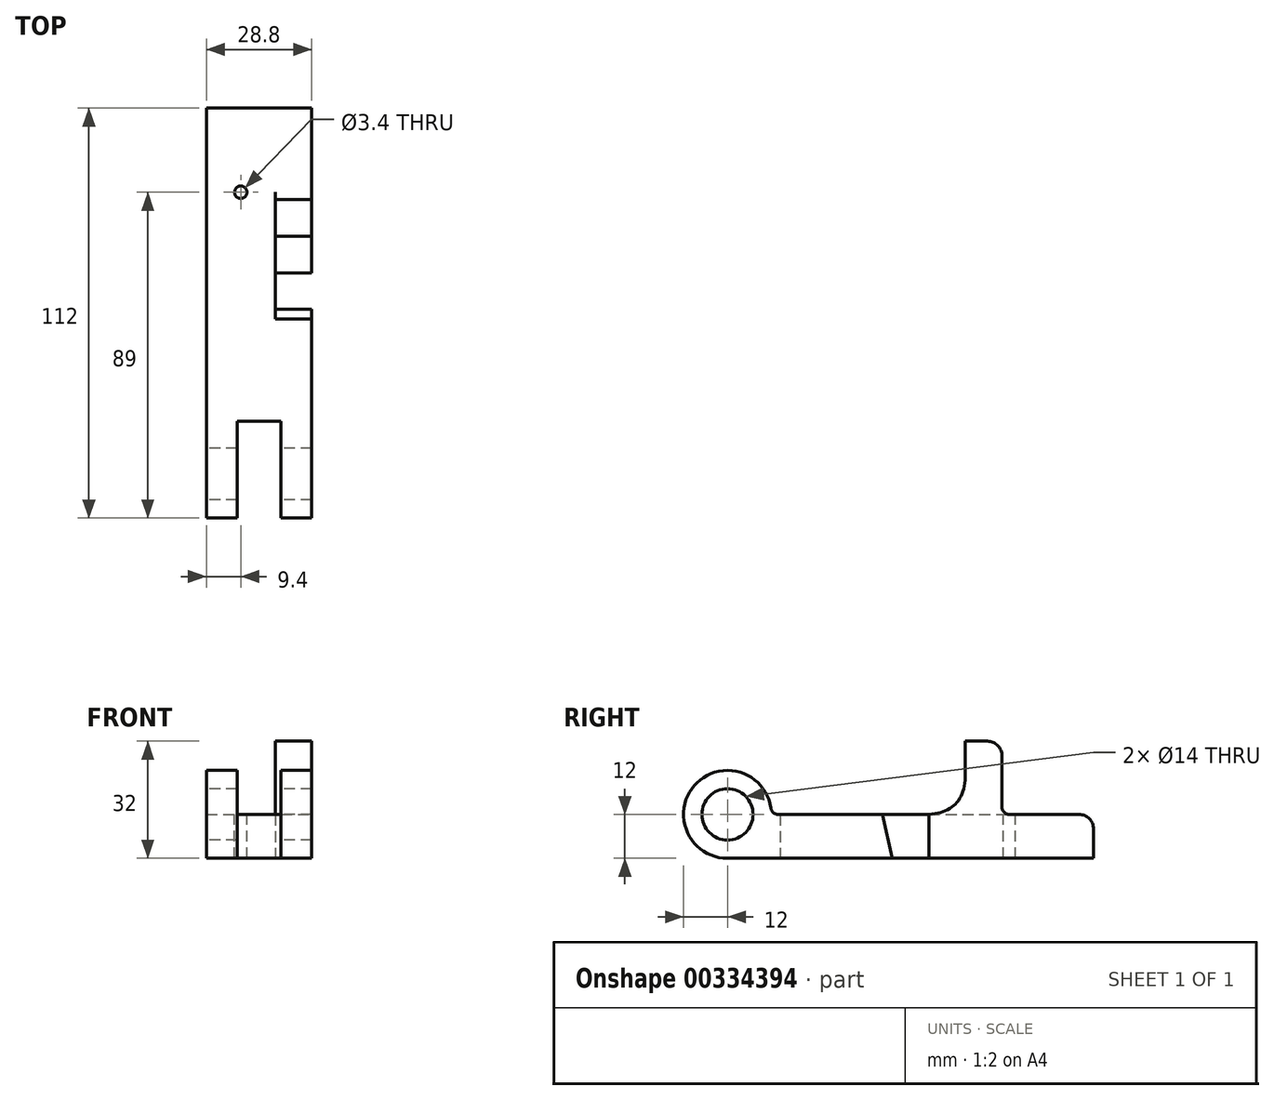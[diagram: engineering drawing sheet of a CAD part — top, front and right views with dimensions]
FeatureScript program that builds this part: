
annotation { "Feature Type Name" : "Feature", "Feature Type Description" : "" }
export const myFeature = defineFeature(function(context is Context, id is Id, definition is map)
    precondition{}
    {
        {
            var Q0;
            Q0=qCreatedBy(makeId("Right.planeOp"),FACE);
            var sketch = newSketch(context, id + "F0", { "sketchPlane" : qUnion([Q0])});
            skArc(sketch, "E0", {"start": v(12, 0) * mm, "mid": v(-8.49, 8.49) * mm, "end": v(0, -12) * mm});
            skCircle(sketch, "E1", {"center": v(0, 0) * mm, "radius": 7 * mm});
            skLineSegment(sketch, "E2", {"start": v(0, -12) * mm, "end": v(47.36, -12) * mm});
            skLineSegment(sketch, "E3", {"start": v(47.36, -12) * mm, "end": v(57.36, -12) * mm});
            skLineSegment(sketch, "E4", {"start": v(57.36, -12) * mm, "end": v(100, -12) * mm});
            skLineSegment(sketch, "E5", {"start": v(100, -12) * mm, "end": v(100, -4) * mm});
            skLineSegment(sketch, "E6", {"start": v(96, 0) * mm, "end": v(77, 0) * mm});
            skLineSegment(sketch, "E7", {"start": v(0, 12) * mm, "end": v(42.36, 12) * mm, "construction": true});
            skLineSegment(sketch, "E8", {"start": v(42.36, 0) * mm, "end": v(47.36, -12) * mm});
            skLineSegment(sketch, "E9", {"start": v(57.36, -12) * mm, "end": v(57.36, 0) * mm});
            skLineSegment(sketch, "E10", {"start": v(65, 20) * mm, "end": v(71, 20) * mm});
            skLineSegment(sketch, "E11", {"start": v(75, 16) * mm, "end": v(75, 2) * mm});
            skPoint(sketch, "E12.visualSharp", {"position": v(100, 0) * mm});
            skArc(sketch, "E12.filletArc", {"start": v(100, -4) * mm, "mid": v(98.83, -1.17) * mm, "end": v(96, 0) * mm});
            skPoint(sketch, "E13.visualSharp", {"position": v(75, 20) * mm});
            skArc(sketch, "E13.filletArc", {"start": v(75, 16) * mm, "mid": v(73.83, 18.83) * mm, "end": v(71, 20) * mm});
            skLineSegment(sketch, "E14.trimOffspring", {"start": v(57.36, 0) * mm, "end": v(12, 0) * mm});
            skPoint(sketch, "E15.visualSharp", {"position": v(75, 0) * mm});
            skArc(sketch, "E15.filletArc", {"start": v(75, 2) * mm, "mid": v(75.59, 0.59) * mm, "end": v(77, 0) * mm});
            skLineSegment(sketch, "E16", {"start": v(65, 20) * mm, "end": v(65, 0) * mm});
            skLineSegment(sketch, "E17", {"start": v(57.36, 0) * mm, "end": v(65, 0) * mm});
            skSolve(sketch);
        }
        {
            var Q0;
            {var subQ1=sQuery(id+"F0.wireOp",EDGE,"E0");Q0=makeQuery(id+"F0.imprint","IMPRINT",FACE,{"disambiguationData":[TD([[makeQuery(id+"F0.imprint","IMPRINT",EDGE,{"derivedFrom":subQ1}),1.0]])]});}
            var Q1;
            Q1=makeQuery(id+"F0.imprint","IMPRINT",FACE,{"disambiguationData":[TD([[makeQuery(id+"F0.imprint","IMPRINT",EDGE,{"derivedFrom":sQuery(id+"F0.wireOp",EDGE,"E3")}),1.0]])]});
            var Q2;
            Q2=makeQuery(id+"F0.imprint","IMPRINT",FACE,{"disambiguationData":[TD([[makeQuery(id+"F0.imprint","IMPRINT",EDGE,{"derivedFrom":sQuery(id+"F0.wireOp",EDGE,"E4")}),1.0]])]});
            extrude(context, id + "F1", {"entities" : qUnion([Q0, Q1, Q2]), "endBound" : BoundingType.SYMMETRIC, "depth" : 28.8 * mm});
        }
        {
            var Q0;
            Q0=makeQuery(id+"F1.opExtrude","SWEPT_FACE",FACE,{"disambiguationData":[OSD([sQuery(id+"F0.wireOp",EDGE,"E14.trimOffspring"),sQuery(id+"F0.wireOp",EDGE,"E17")])]});
            var sketch = newSketch(context, id + "F2", { "sketchPlane" : qUnion([Q0])});
            skLineSegment(sketch, "E18.bottom", {"start": v(6, 14.45) * mm, "end": v(-6, 14.45) * mm});
            skLineSegment(sketch, "E18.top", {"start": v(6, -14.45) * mm, "end": v(-6, -14.45) * mm});
            skLineSegment(sketch, "E18.left", {"start": v(6, 14.45) * mm, "end": v(6, -14.45) * mm});
            skLineSegment(sketch, "E18.right", {"start": v(-6, 14.45) * mm, "end": v(-6, -14.45) * mm});
            skPoint(sketch, "E18.middle", {"position": v(0, 0) * mm});
            skSolve(sketch);
        }
        {
            var Q0;
            {var subQ0=sQuery(id+"F2.wireOp",EDGE,"E18.top");Q0=makeQuery(id+"F2.imprint","IMPRINT",FACE,{"disambiguationData":[TD([[makeQuery(id+"F2.imprint","IMPRINT",EDGE,{"derivedFrom":subQ0}),-1.0]])]});}
            var Q1;
            {var subQ0=sQuery(id+"F2.wireOp",EDGE,"E18.bottom");Q1=makeQuery(id+"F2.imprint","IMPRINT",FACE,{"disambiguationData":[TD([[makeQuery(id+"F2.imprint","IMPRINT",EDGE,{"derivedFrom":subQ0}),1.0]])]});}
            extrude(context, id + "F3", {"entities" : qUnion([Q0, Q1]), "operationType" : NewBodyOperationType.REMOVE, "endBound" : BoundingType.SYMMETRIC, "depth" : 30 * mm});
        }
        {
            var Q0;
            {var subQ0=sQuery(id+"F0.wireOp",EDGE,"E0");var subQ2=sQuery(id+"F0.wireOp",EDGE,"E14.trimOffspring");Q0=makeQuery(id+"F3.boolean.opBoolean","SPLIT",EDGE,{"disambiguationData":[TD([makeQuery(id+"F3.opExtrude","SWEPT_FACE",FACE,{"disambiguationData":[OSD([sQuery(id+"F2.wireOp",EDGE,"E18.left")])]})])],"derivedFrom":makeQuery(id+"F1.opExtrude","SWEPT_EDGE",EDGE,{"disambiguationData":[OSD([subQ0,subQ2])]})});}
            var Q1;
            {var subQ0=sQuery(id+"F0.wireOp",EDGE,"E0");var subQ2=sQuery(id+"F0.wireOp",EDGE,"E14.trimOffspring");Q1=makeQuery(id+"F3.boolean.opBoolean","SPLIT",EDGE,{"disambiguationData":[TD([makeQuery(id+"F3.opExtrude","SWEPT_FACE",FACE,{"disambiguationData":[OSD([sQuery(id+"F2.wireOp",EDGE,"E18.right")])]})])],"derivedFrom":makeQuery(id+"F1.opExtrude","SWEPT_EDGE",EDGE,{"disambiguationData":[OSD([subQ0,subQ2])]})});}
            fillet(context, id + "F4", {"entities" : qUnion([Q0, Q1]), "radius" : 2 * mm, "tangentPropagation" : true, "allowEdgeOverflow" : false});
        }
        {
            var Q0;
            Q0=makeQuery(id+"F1.opExtrude","SWEPT_FACE",FACE,{"disambiguationData":[OSD([sQuery(id+"F0.wireOp",EDGE,"E6")])]});
            var sketch = newSketch(context, id + "F5", { "sketchPlane" : qUnion([Q0])});
            skLineSegment(sketch, "E19", {"start": v(-14.4, 100) * mm, "end": v(-14.4, 77) * mm, "construction": true});
            skLineSegment(sketch, "E20", {"start": v(-14.4, 100) * mm, "end": v(-14.4, 90.6) * mm, "construction": true});
            skLineSegment(sketch, "E21", {"start": v(-14.4, 77) * mm, "end": v(-5, 77) * mm});
            skCircle(sketch, "E22", {"center": v(-5, 77) * mm, "radius": 1.7 * mm});
            skSolve(sketch);
        }
        {
            var Q0;
            {var subQ0=sQuery(id+"F5.wireOp",EDGE,"E21");var subQ3=sQuery(id+"F5.wireOp",EDGE,"E22");var subQ4=makeQuery(id+"F5.imprint","INTERSECT",VERTEX,{"derivedFrom":[subQ0,subQ3]});Q0=makeQuery(id+"F5.imprint","IMPRINT",FACE,{"disambiguationData":[TD([[makeQuery(id+"F5.imprint","IMPRINT",EDGE,{"disambiguationData":[TD([[subQ4,1.0]])],"derivedFrom":subQ0}),1.0]])]});}
            var Q1;
            {var subQ0=sQuery(id+"F5.wireOp",EDGE,"E21");var subQ3=sQuery(id+"F5.wireOp",EDGE,"E22");var subQ4=makeQuery(id+"F5.imprint","INTERSECT",VERTEX,{"derivedFrom":[subQ0,subQ3]});Q1=makeQuery(id+"F5.imprint","IMPRINT",FACE,{"disambiguationData":[TD([[makeQuery(id+"F5.imprint","IMPRINT",EDGE,{"disambiguationData":[TD([[subQ4,1.0]])],"derivedFrom":subQ0}),-1.0]])]});}
            extrude(context, id + "F6", {"entities" : qUnion([Q0, Q1]), "operationType" : NewBodyOperationType.REMOVE, "oppositeDirection" : true, "depth" : 25 * mm});
        }
        {
            var Q0;
            Q0=makeQuery(id+"F1.opExtrude","SWEPT_FACE",FACE,{"disambiguationData":[OSD([sQuery(id+"F0.wireOp",EDGE,"E14.trimOffspring"),sQuery(id+"F0.wireOp",EDGE,"E17")])]});
            var sketch = newSketch(context, id + "F7", { "sketchPlane" : qUnion([Q0])});
            skLineSegment(sketch, "E23.bottom", {"start": v(-14.4, 51.43) * mm, "end": v(4.4, 51.43) * mm});
            skLineSegment(sketch, "E23.top", {"start": v(-14.4, 98.23) * mm, "end": v(4.4, 98.23) * mm});
            skLineSegment(sketch, "E23.left", {"start": v(-14.4, 51.43) * mm, "end": v(-14.4, 98.23) * mm});
            skLineSegment(sketch, "E23.right", {"start": v(4.4, 51.43) * mm, "end": v(4.4, 98.23) * mm});
            skSolve(sketch);
        }
        {
            var Q0;
            {var subQ0=sQuery(id+"F7.wireOp",EDGE,"E23.top");Q0=makeQuery(id+"F7.imprint","IMPRINT",FACE,{"disambiguationData":[TD([[makeQuery(id+"F7.imprint","IMPRINT",EDGE,{"derivedFrom":subQ0}),-1.0]])]});}
            var Q1;
            {var subQ0=sQuery(id+"F7.wireOp",EDGE,"E23.bottom");Q1=makeQuery(id+"F7.imprint","IMPRINT",FACE,{"disambiguationData":[TD([[makeQuery(id+"F7.imprint","IMPRINT",EDGE,{"derivedFrom":subQ0}),1.0]])]});}
            extrude(context, id + "F8", {"entities" : qUnion([Q0, Q1]), "operationType" : NewBodyOperationType.REMOVE, "depth" : 25 * mm});
        }
        {
            var Q0;
            Q0=makeQuery(id+"F8.boolean.opBoolean","MERGE",FACE,{"derivedFrom":[makeQuery(id+"F1.opExtrude","SWEPT_FACE",FACE,{"disambiguationData":[OSD([sQuery(id+"F0.wireOp",EDGE,"E14.trimOffspring"),sQuery(id+"F0.wireOp",EDGE,"E17")])]}),makeQuery(id+"F1.opExtrude","SWEPT_FACE",FACE,{"disambiguationData":[OSD([sQuery(id+"F0.wireOp",EDGE,"E6")])]}),makeQuery(id+"F8.opExtrude","CAP_FACE",FACE,{"disambiguationData":[OSD([sQuery(id+"F7.wireOp",EDGE,"E23.bottom"),sQuery(id+"F7.wireOp",EDGE,"E23.top"),sQuery(id+"F7.wireOp",EDGE,"E23.left"),sQuery(id+"F7.wireOp",EDGE,"E23.right")])],"isStart":true})]});
            var sketch = newSketch(context, id + "F9", { "sketchPlane" : qUnion([Q0])});
            skLineSegment(sketch, "E24.bottom", {"start": v(14.4, 65) * mm, "end": v(4.4, 65) * mm});
            skLineSegment(sketch, "E24.top", {"start": v(14.4, 44.64) * mm, "end": v(4.4, 44.64) * mm});
            skLineSegment(sketch, "E24.left", {"start": v(14.4, 65) * mm, "end": v(14.4, 44.64) * mm});
            skLineSegment(sketch, "E24.right", {"start": v(4.4, 65) * mm, "end": v(4.4, 44.64) * mm});
            skSolve(sketch);
        }
        {
            var Q0;
            Q0=makeQuery(id+"F1.opExtrude","CAP_FACE",FACE,{"disambiguationData":[OSD([sQuery(id+"F0.wireOp",EDGE,"E0"),sQuery(id+"F0.wireOp",EDGE,"E1"),sQuery(id+"F0.wireOp",EDGE,"E2"),sQuery(id+"F0.wireOp",EDGE,"E3"),sQuery(id+"F0.wireOp",EDGE,"E4"),sQuery(id+"F0.wireOp",EDGE,"E5"),sQuery(id+"F0.wireOp",EDGE,"E6"),sQuery(id+"F0.wireOp",EDGE,"E10"),sQuery(id+"F0.wireOp",EDGE,"E11"),sQuery(id+"F0.wireOp",EDGE,"E12.filletArc"),sQuery(id+"F0.wireOp",EDGE,"E13.filletArc"),sQuery(id+"F0.wireOp",EDGE,"E14.trimOffspring"),sQuery(id+"F0.wireOp",EDGE,"E15.filletArc"),sQuery(id+"F0.wireOp",EDGE,"E16"),sQuery(id+"F0.wireOp",EDGE,"E17")])],"isStart":false});
            var sketch = newSketch(context, id + "F10", { "sketchPlane" : qUnion([Q0])});
            skLineSegment(sketch, "E25", {"start": v(55, 0) * mm, "end": v(55, -12) * mm});
            skLineSegment(sketch, "E26", {"start": v(55, -12) * mm, "end": v(45, -12) * mm});
            skLineSegment(sketch, "E27", {"start": v(55, 0) * mm, "end": v(42.36, 0) * mm});
            skLineSegment(sketch, "E28", {"start": v(42.36, 0) * mm, "end": v(45, -12) * mm});
            skSolve(sketch);
        }
        {
            var Q0;
            Q0=makeQuery(id+"F10.imprint","IMPRINT",FACE,{"disambiguationData":[TD([[makeQuery(id+"F10.imprint","IMPRINT",EDGE,{"derivedFrom":sQuery(id+"F10.wireOp",EDGE,"E25")}),-1.0]])]});
            extrude(context, id + "F11", {"entities" : qUnion([Q0]), "operationType" : NewBodyOperationType.REMOVE, "oppositeDirection" : true, "depth" : 10 * mm});
        }
        {
            var Q0;
            Q0=makeQuery(id+"F1.opExtrude","SWEPT_EDGE",EDGE,{"disambiguationData":[OSD([sQuery(id+"F0.wireOp",EDGE,"E16"),sQuery(id+"F0.wireOp",EDGE,"E17")])]});
            fillet(context, id + "F12", {"entities" : qUnion([Q0]), "radius" : 11.1 * mm, "rho" : 0.5, "crossSection" : FilletCrossSection.CONIC, "allowEdgeOverflow" : false});
        }
    });
